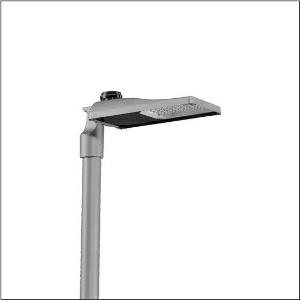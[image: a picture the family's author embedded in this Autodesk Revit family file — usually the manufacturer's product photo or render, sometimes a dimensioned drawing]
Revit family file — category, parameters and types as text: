
# Revit family: streetlight_sl_31_mini___st1_0a_5xh6d3bn08ja_1c18
name_source: partatom
category: Lighting Fixtures
units: mm (PartAtom-declared; Revit-internal decimal feet)

## family parameters
Cut with Voids When Loaded = No
Host = Face
Light Source = No
Part Type = Normal
Room Calculation Point = No
Round Connector Dimension = Use Diameter
Shared = No

## types (1)
- --- (1 x LED, 12140 lm, 81.1 W, 3000K)
    Apparent Load = 81 VA
    CIE Flux Codes = 40 73 97 100 100
    Color Rendering = 70
    Color Temperature = 3000K
    Default Elevation = 1800 mm
    Description = Streetlight SL 31 mini NEMA (7pin) mast luminaire for post-top, side-entry; light control with lens of PMMA; light distribution: ST1.0a, direct asymmetric distribution, for standard-compliant lighting for roads and squares; LED: luminous flux: 12.140lm, light colour: 730, colour temperature: 3000K; luminous efficacy: 149,7lm/W; control: pre-setting: linear dimming characteristic, flexible luminous flux parameterisation, time-dependent luminous flux control, constant luminous flux control, intelligent temperature release in ECG and LED module, overheat protection; luminaire housing, of diecast aluminium, Siteco® metallic grey (DB 702S), corrosivity category C5 high according to DIN EN ISO 12944; cover of toughened safety glass, transparent, opened without tools; mast flange of diecast aluminium, Siteco® metallic grey (DB 702S), spigot size: 76/60mm, mast flange included unmounted; with cable H07RN-F 3x 1.5mm², cable length: 10,5m, connection cable pre-assembled; mains connection: 220..240V, AC, 50/60Hz; power consumption (at start of service life): 81,1W / (at end of service life): 88,3W / (with reduced operation 50%): 36,4W; protection rating (complete): IP66; insulation class (complete): insulation class I (protective earthing); impact resistance: IK10; certification: CE, ENEC, ENEC+, VDE, UKCA; permissible operating ambient temperature for outdoor applications: -40..+50°C; packaging unit: 1 piece

Light Distribution: ST1.0a
    Height = 76 mm
    Lamp = 1 x LED
    Lamp Light Flux = 12140 lm
    Lamp Power = 81.1 W
    Lamp count = 1
    Length = 547 mm
    Luminous efficacy = 150 lm/W
    Manufacturer = Siteco
    ModVariant = No
    Model = 5XH6D3BN08JA
    Number of Poles = 1
    OnlyDefault = Yes
    Power Factor = 1
    Product Name = Streetlight SL 31 mini | ST1.0a
    Product group = mast luminaire | pylon top
    ProductGroupID = 6100
    Protection Class = Protection class I
    Protection Degree = IP 66
    RLX_Detail_Level = 1
    RLX_Emergency_Light_Flux = 0 lm
    RLX_Emergency_Type = 0
    RLX_Emergency_Type_DB = No
    RlxData = <blob elided: 40273 chars, md5=4f3b990e>
    Socket = socket
    Standby Power = 0 W
    System Light Flux = 12140 lm
    System Power = 81 W
    Type Comments = factory setting: luminous flux: 100 % | dim-lin: 254 | 860 mA
    Type Image = l_1300322.jpg
    URL = http://relux.com
    VarID = @adj_050086
    Voltage = 0 V
    Weight = 0.00 kg
    Width = 265 mm

## geometry (parser evidence)
native form markers: Blend x4, Sweep x10
no freeform markers — native parametric forms only
